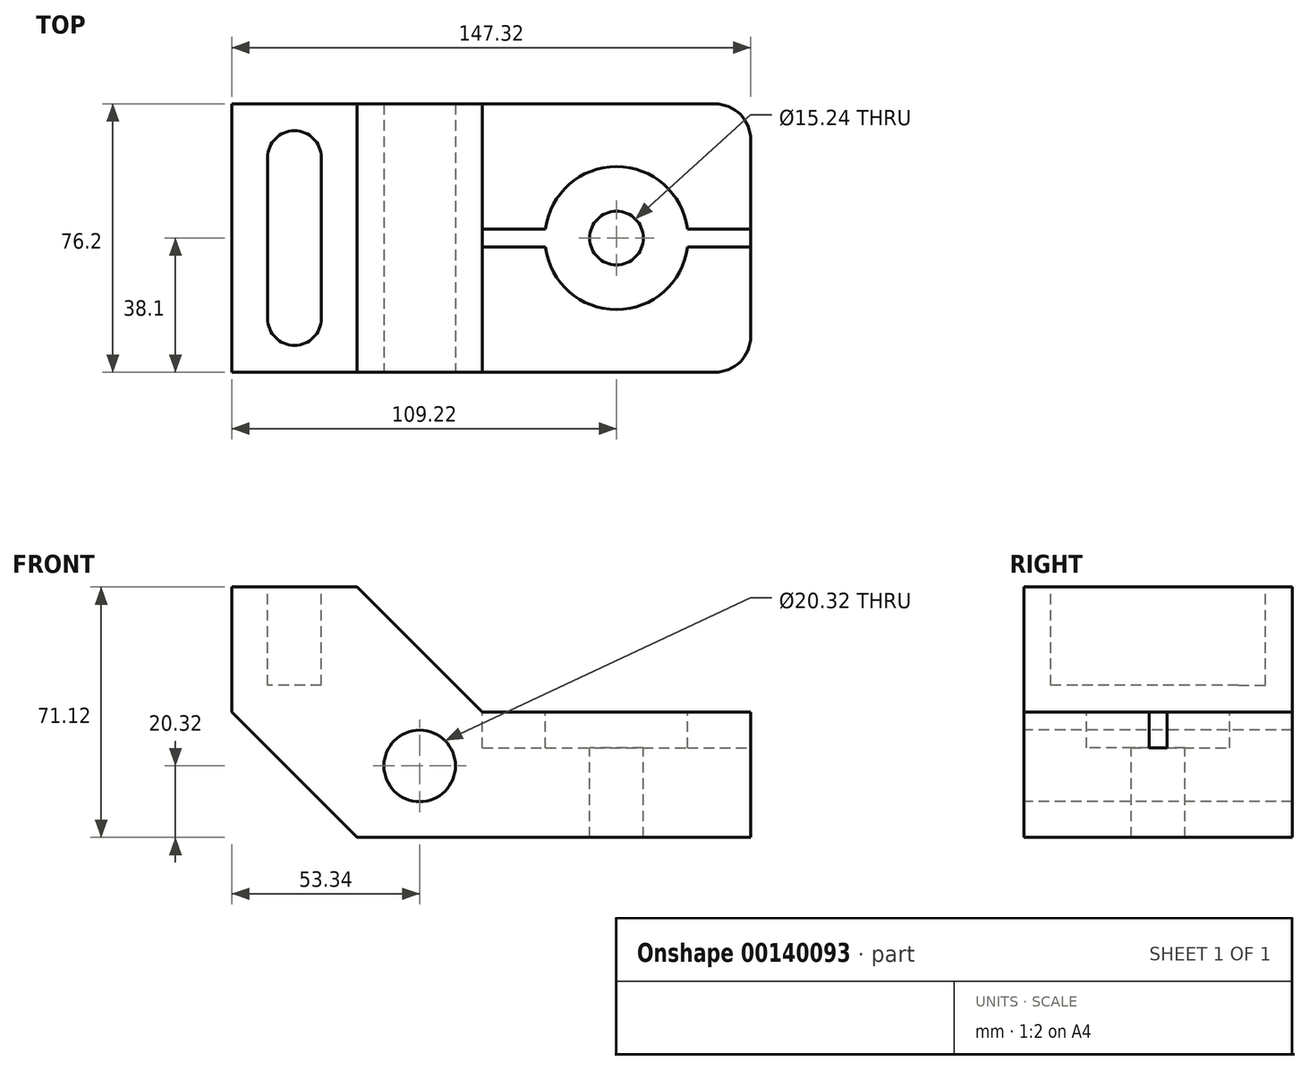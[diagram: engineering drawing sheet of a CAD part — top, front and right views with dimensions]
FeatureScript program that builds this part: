
annotation { "Feature Type Name" : "Feature", "Feature Type Description" : "" }
export const myFeature = defineFeature(function(context is Context, id is Id, definition is map)
    precondition{}
    {
        {
            var Q0;
            Q0=qCreatedBy(makeId("Top.planeOp"),FACE);
            var sketch = newSketch(context, id + "F0", { "sketchPlane" : qUnion([Q0])});
            skLineSegment(sketch, "E0.bottom", {"start": v(0, 0) * mm, "end": v(147.32, 0) * mm});
            skLineSegment(sketch, "E0.top", {"start": v(0, -76.2) * mm, "end": v(147.32, -76.2) * mm});
            skLineSegment(sketch, "E0.left", {"start": v(0, 0) * mm, "end": v(0, -76.2) * mm});
            skLineSegment(sketch, "E0.right", {"start": v(147.32, 0) * mm, "end": v(147.32, -76.2) * mm});
            skSolve(sketch);
        }
        {
            var Q0;
            Q0 = qSketchRegion(id + "F0", true);
            extrude(context, id + "F1", {"entities" : qUnion([Q0]), "depth" : 71.12 * mm});
        }
        {
            var Q0;
            Q0=makeQuery(id+"F1.opExtrude","SWEPT_EDGE",EDGE,{"disambiguationData":[OSD([sQuery(id+"F0.wireOp",EDGE,"E0.bottom"),sQuery(id+"F0.wireOp",EDGE,"E0.right")])]});
            var Q1;
            Q1=makeQuery(id+"F1.opExtrude","SWEPT_EDGE",EDGE,{"disambiguationData":[OSD([sQuery(id+"F0.wireOp",EDGE,"E0.top"),sQuery(id+"F0.wireOp",EDGE,"E0.right")])]});
            fillet(context, id + "F2", {"entities" : qUnion([Q0, Q1]), "radius" : 10.16 * mm, "tangentPropagation" : true, "allowEdgeOverflow" : false});
        }
        {
            var Q0;
            Q0=makeQuery(id+"F1.opExtrude","SWEPT_FACE",FACE,{"disambiguationData":[OSD([sQuery(id+"F0.wireOp",EDGE,"E0.top")])]});
            var sketch = newSketch(context, id + "F3", { "sketchPlane" : qUnion([Q0])});
            skLineSegment(sketch, "E1", {"start": v(0, 35.56) * mm, "end": v(35.56, 0) * mm});
            skLineSegment(sketch, "E2", {"start": v(35.56, 0) * mm, "end": v(0, 0) * mm});
            skLineSegment(sketch, "E3", {"start": v(0, 0) * mm, "end": v(0, 35.56) * mm});
            skLineSegment(sketch, "E4", {"start": v(35.56, 71.12) * mm, "end": v(71.12, 35.56) * mm});
            skPoint(sketch, "E4.endSnap0", {"position": v(137.16, 35.56) * mm});
            skLineSegment(sketch, "E5", {"start": v(71.12, 35.56) * mm, "end": v(147.32, 35.56) * mm});
            skLineSegment(sketch, "E6", {"start": v(147.32, 35.56) * mm, "end": v(147.32, 71.12) * mm});
            skPoint(sketch, "E6.endSnap0", {"position": v(68.58, 71.12) * mm});
            skLineSegment(sketch, "E7", {"start": v(147.32, 71.12) * mm, "end": v(35.56, 71.12) * mm});
            skCircle(sketch, "E8", {"center": v(53.34, 20.32) * mm, "radius": 10.16 * mm});
            skSolve(sketch);
        }
        {
            var Q0;
            Q0 = qSketchRegion(id + "F3", true);
            extrude(context, id + "F4", {"entities" : qUnion([Q0]), "operationType" : NewBodyOperationType.REMOVE, "endBound" : BoundingType.THROUGH_ALL, "oppositeDirection" : true, "depth" : 25.4 * mm});
        }
        {
            var Q0;
            Q0=makeQuery(id+"F1.opExtrude","CAP_FACE",FACE,{"disambiguationData":[OSD([sQuery(id+"F0.wireOp",EDGE,"E0.bottom"),sQuery(id+"F0.wireOp",EDGE,"E0.top"),sQuery(id+"F0.wireOp",EDGE,"E0.left"),sQuery(id+"F0.wireOp",EDGE,"E0.right")])],"isStart":false});
            var sketch = newSketch(context, id + "F5", { "sketchPlane" : qUnion([Q0])});
            skArc(sketch, "E9", {"start": v(25.4, -15.24) * mm, "mid": v(17.78, -7.62) * mm, "end": v(10.16, -15.24) * mm});
            skArc(sketch, "E10", {"start": v(10.16, -60.96) * mm, "mid": v(17.78, -68.58) * mm, "end": v(25.4, -60.96) * mm});
            skLineSegment(sketch, "E11.left", {"start": v(10.16, -15.24) * mm, "end": v(10.16, -60.96) * mm});
            skLineSegment(sketch, "E11.right", {"start": v(25.4, -15.24) * mm, "end": v(25.4, -60.96) * mm});
            skSolve(sketch);
        }
        {
            var Q0;
            Q0 = qSketchRegion(id + "F5", true);
            extrude(context, id + "F6", {"entities" : qUnion([Q0]), "operationType" : NewBodyOperationType.REMOVE, "oppositeDirection" : true, "depth" : 27.94 * mm});
        }
        {
            var Q0;
            Q0=makeQuery(id+"F4.boolean.opBoolean","COPY",FACE,{"derivedFrom":makeQuery(id+"F4.opExtrude","SWEPT_FACE",FACE,{"disambiguationData":[OSD([sQuery(id+"F3.wireOp",EDGE,"E5")])]})});
            var sketch = newSketch(context, id + "F7", { "sketchPlane" : qUnion([Q0])});
            skCircle(sketch, "E12", {"center": v(109.22, -38.1) * mm, "radius": 7.62 * mm});
            skSolve(sketch);
        }
        {
            var Q0;
            Q0 = qSketchRegion(id + "F7", true);
            extrude(context, id + "F8", {"entities" : qUnion([Q0]), "operationType" : NewBodyOperationType.REMOVE, "endBound" : BoundingType.THROUGH_ALL, "oppositeDirection" : true, "depth" : 25.4 * mm});
        }
        {
            var Q0;
            Q0=makeQuery(id+"F4.boolean.opBoolean","COPY",FACE,{"derivedFrom":makeQuery(id+"F4.opExtrude","SWEPT_FACE",FACE,{"disambiguationData":[OSD([sQuery(id+"F3.wireOp",EDGE,"E5")])]})});
            var sketch = newSketch(context, id + "F9", { "sketchPlane" : qUnion([Q0])});
            skCircle(sketch, "E13", {"center": v(109.22, -38.1) * mm, "radius": 20.32 * mm});
            skLineSegment(sketch, "E14.bottom", {"start": v(71.12, -35.56) * mm, "end": v(147.32, -35.56) * mm});
            skLineSegment(sketch, "E14.top", {"start": v(71.12, -40.64) * mm, "end": v(147.32, -40.64) * mm});
            skLineSegment(sketch, "E14.left", {"start": v(71.12, -35.56) * mm, "end": v(71.12, -40.64) * mm});
            skLineSegment(sketch, "E14.right", {"start": v(147.32, -35.56) * mm, "end": v(147.32, -40.64) * mm});
            skSolve(sketch);
        }
        {
            var Q0;
            Q0 = qSketchRegion(id + "F9", true);
            extrude(context, id + "F10", {"entities" : qUnion([Q0]), "operationType" : NewBodyOperationType.REMOVE, "oppositeDirection" : true, "depth" : 10.16 * mm});
        }
    });
